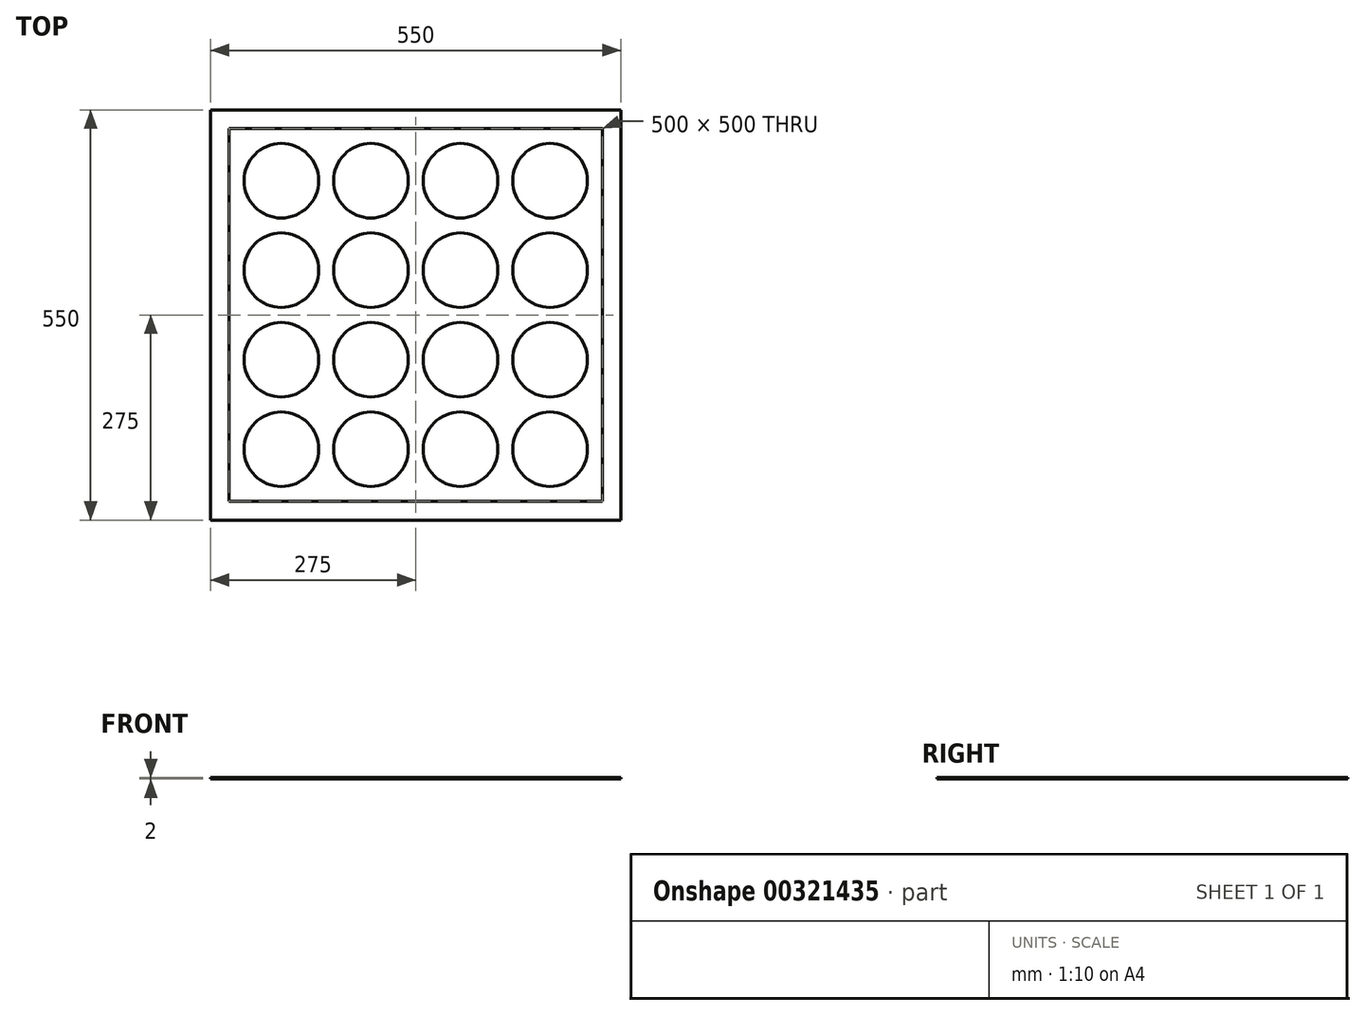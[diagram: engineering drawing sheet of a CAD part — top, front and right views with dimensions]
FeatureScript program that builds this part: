
annotation { "Feature Type Name" : "Feature", "Feature Type Description" : "" }
export const myFeature = defineFeature(function(context is Context, id is Id, definition is map)
    precondition{}
    {
        {
            var Q0;
            Q0=qCreatedBy(makeId("Top.planeOp"),FACE);
            var sketch = newSketch(context, id + "F0", { "sketchPlane" : qUnion([Q0])});
            skLineSegment(sketch, "E0.bottom", {"start": v(-250, 250) * mm, "end": v(250, 250) * mm});
            skLineSegment(sketch, "E0.top", {"start": v(-250, -250) * mm, "end": v(250, -250) * mm});
            skLineSegment(sketch, "E0.left", {"start": v(-250, 250) * mm, "end": v(-250, -250) * mm});
            skLineSegment(sketch, "E0.right", {"start": v(250, 250) * mm, "end": v(250, -250) * mm});
            skPoint(sketch, "E0.middle", {"position": v(0, 0) * mm});
            skCircle(sketch, "E1", {"center": v(-180, 180) * mm, "radius": 50 * mm});
            skCircle(sketch, "E2.0.1.0", {"center": v(-180, 60) * mm, "radius": 50 * mm});
            skCircle(sketch, "E2.0.2.0", {"center": v(-180, -60) * mm, "radius": 50 * mm});
            skCircle(sketch, "E2.0.3.0", {"center": v(-180, -180) * mm, "radius": 50 * mm});
            skCircle(sketch, "E2.1.0.0", {"center": v(-60, 180) * mm, "radius": 50 * mm});
            skCircle(sketch, "E2.1.1.0", {"center": v(-60, 60) * mm, "radius": 50 * mm});
            skCircle(sketch, "E2.1.2.0", {"center": v(-60, -60) * mm, "radius": 50 * mm});
            skCircle(sketch, "E2.1.3.0", {"center": v(-60, -180) * mm, "radius": 50 * mm});
            skCircle(sketch, "E2.2.0.0", {"center": v(60, 180) * mm, "radius": 50 * mm});
            skCircle(sketch, "E2.2.1.0", {"center": v(60, 60) * mm, "radius": 50 * mm});
            skCircle(sketch, "E2.2.2.0", {"center": v(60, -60) * mm, "radius": 50 * mm});
            skCircle(sketch, "E2.2.3.0", {"center": v(60, -180) * mm, "radius": 50 * mm});
            skCircle(sketch, "E2.3.0.0", {"center": v(180, 180) * mm, "radius": 50 * mm});
            skCircle(sketch, "E2.3.1.0", {"center": v(180, 60) * mm, "radius": 50 * mm});
            skCircle(sketch, "E2.3.2.0", {"center": v(180, -60) * mm, "radius": 50 * mm});
            skCircle(sketch, "E2.3.3.0", {"center": v(180, -180) * mm, "radius": 50 * mm});
            skLineSegment(sketch, "E2.direction1", {"start": v(-180, 180) * mm, "end": v(-60, 180) * mm, "construction": true});
            skLineSegment(sketch, "E2.direction2", {"start": v(-180, 180) * mm, "end": v(-180, 60) * mm, "construction": true});
            skLineSegment(sketch, "E3", {"start": v(60, -60) * mm, "end": v(-60, 60) * mm, "construction": true});
            skLineSegment(sketch, "E4.0", {"start": v(-275, 275) * mm, "end": v(275, 275) * mm});
            skLineSegment(sketch, "E4.1", {"start": v(-275, 275) * mm, "end": v(-275, -275) * mm});
            skLineSegment(sketch, "E4.2", {"start": v(-275, -275) * mm, "end": v(275, -275) * mm});
            skLineSegment(sketch, "E4.3", {"start": v(275, 275) * mm, "end": v(275, -275) * mm});
            skSolve(sketch);
        }
        {
            var Q0;
            Q0 = qSketchRegion(id + "F0", true);
            var Q1;
            Q1=makeQuery(id+"F0.imprint","IMPRINT",FACE,{"disambiguationData":[TD([[makeQuery(id+"F0.imprint","IMPRINT",EDGE,{"derivedFrom":sQuery(id+"F0.wireOp",EDGE,"E1")}),1.0]])]});
            var Q2;
            Q2=makeQuery(id+"F0.imprint","IMPRINT",FACE,{"disambiguationData":[TD([[makeQuery(id+"F0.imprint","IMPRINT",EDGE,{"derivedFrom":sQuery(id+"F0.wireOp",EDGE,"E2.1.0.0")}),1.0]])]});
            var Q3;
            Q3=makeQuery(id+"F0.imprint","IMPRINT",FACE,{"disambiguationData":[TD([[makeQuery(id+"F0.imprint","IMPRINT",EDGE,{"derivedFrom":sQuery(id+"F0.wireOp",EDGE,"E2.2.0.0")}),1.0]])]});
            var Q4;
            Q4=makeQuery(id+"F0.imprint","IMPRINT",FACE,{"disambiguationData":[TD([[makeQuery(id+"F0.imprint","IMPRINT",EDGE,{"derivedFrom":sQuery(id+"F0.wireOp",EDGE,"E2.3.0.0")}),1.0]])]});
            var Q5;
            Q5=makeQuery(id+"F0.imprint","IMPRINT",FACE,{"disambiguationData":[TD([[makeQuery(id+"F0.imprint","IMPRINT",EDGE,{"derivedFrom":sQuery(id+"F0.wireOp",EDGE,"E2.3.1.0")}),1.0]])]});
            var Q6;
            Q6=makeQuery(id+"F0.imprint","IMPRINT",FACE,{"disambiguationData":[TD([[makeQuery(id+"F0.imprint","IMPRINT",EDGE,{"derivedFrom":sQuery(id+"F0.wireOp",EDGE,"E2.2.1.0")}),1.0]])]});
            var Q7;
            Q7=makeQuery(id+"F0.imprint","IMPRINT",FACE,{"disambiguationData":[TD([[makeQuery(id+"F0.imprint","IMPRINT",EDGE,{"derivedFrom":sQuery(id+"F0.wireOp",EDGE,"E2.1.1.0")}),1.0]])]});
            var Q8;
            Q8=makeQuery(id+"F0.imprint","IMPRINT",FACE,{"disambiguationData":[TD([[makeQuery(id+"F0.imprint","IMPRINT",EDGE,{"derivedFrom":sQuery(id+"F0.wireOp",EDGE,"E2.0.1.0")}),1.0]])]});
            var Q9;
            Q9=makeQuery(id+"F0.imprint","IMPRINT",FACE,{"disambiguationData":[TD([[makeQuery(id+"F0.imprint","IMPRINT",EDGE,{"derivedFrom":sQuery(id+"F0.wireOp",EDGE,"E2.0.2.0")}),1.0]])]});
            var Q10;
            Q10=makeQuery(id+"F0.imprint","IMPRINT",FACE,{"disambiguationData":[TD([[makeQuery(id+"F0.imprint","IMPRINT",EDGE,{"derivedFrom":sQuery(id+"F0.wireOp",EDGE,"E2.1.2.0")}),1.0]])]});
            var Q11;
            Q11=makeQuery(id+"F0.imprint","IMPRINT",FACE,{"disambiguationData":[TD([[makeQuery(id+"F0.imprint","IMPRINT",EDGE,{"derivedFrom":sQuery(id+"F0.wireOp",EDGE,"E2.2.2.0")}),1.0]])]});
            var Q12;
            Q12=makeQuery(id+"F0.imprint","IMPRINT",FACE,{"disambiguationData":[TD([[makeQuery(id+"F0.imprint","IMPRINT",EDGE,{"derivedFrom":sQuery(id+"F0.wireOp",EDGE,"E2.3.2.0")}),1.0]])]});
            var Q13;
            Q13=makeQuery(id+"F0.imprint","IMPRINT",FACE,{"disambiguationData":[TD([[makeQuery(id+"F0.imprint","IMPRINT",EDGE,{"derivedFrom":sQuery(id+"F0.wireOp",EDGE,"E2.3.3.0")}),1.0]])]});
            var Q14;
            Q14=makeQuery(id+"F0.imprint","IMPRINT",FACE,{"disambiguationData":[TD([[makeQuery(id+"F0.imprint","IMPRINT",EDGE,{"derivedFrom":sQuery(id+"F0.wireOp",EDGE,"E2.2.3.0")}),1.0]])]});
            var Q15;
            Q15=makeQuery(id+"F0.imprint","IMPRINT",FACE,{"disambiguationData":[TD([[makeQuery(id+"F0.imprint","IMPRINT",EDGE,{"derivedFrom":sQuery(id+"F0.wireOp",EDGE,"E2.1.3.0")}),1.0]])]});
            var Q16;
            Q16=makeQuery(id+"F0.imprint","IMPRINT",FACE,{"disambiguationData":[TD([[makeQuery(id+"F0.imprint","IMPRINT",EDGE,{"derivedFrom":sQuery(id+"F0.wireOp",EDGE,"E2.0.3.0")}),1.0]])]});
            extrude(context, id + "F1", {"entities" : qUnion([Q0, Q1, Q2, Q3, Q4, Q5, Q6, Q7, Q8, Q9, Q10, Q11, Q12, Q13, Q14, Q15, Q16]), "depth" : 2 * mm});
        }
    });
